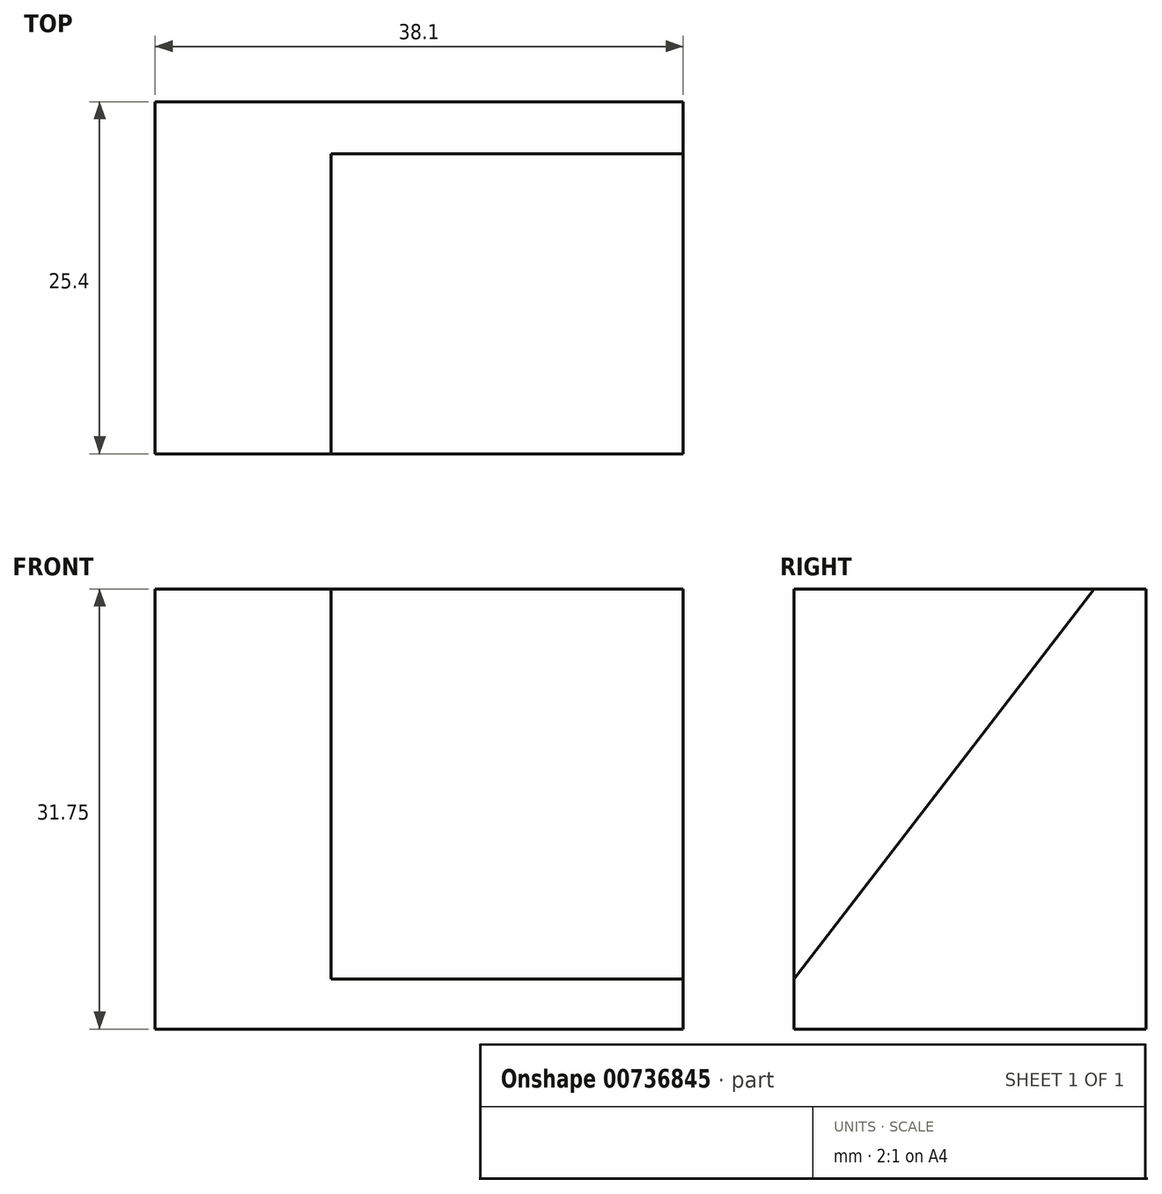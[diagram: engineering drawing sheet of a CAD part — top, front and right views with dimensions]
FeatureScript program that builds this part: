
annotation { "Feature Type Name" : "Feature", "Feature Type Description" : "" }
export const myFeature = defineFeature(function(context is Context, id is Id, definition is map)
    precondition{}
    {
        {
            var Q0;
            Q0=qCreatedBy(makeId("Right.planeOp"),FACE);
            var sketch = newSketch(context, id + "F0", { "sketchPlane" : qUnion([Q0])});
            skLineSegment(sketch, "E0", {"start": v(0, 0) * mm, "end": v(25.4, 0) * mm});
            skLineSegment(sketch, "E1", {"start": v(25.4, 0) * mm, "end": v(25.4, 31.75) * mm});
            skLineSegment(sketch, "E2", {"start": v(25.4, 31.75) * mm, "end": v(0, 31.75) * mm});
            skLineSegment(sketch, "E3", {"start": v(0, 31.75) * mm, "end": v(0, 0) * mm});
            skLineSegment(sketch, "E4", {"start": v(-0.76, 1.48) * mm, "end": v(0, 0) * mm});
            skSolve(sketch);
        }
        {
            var Q0;
            Q0=makeQuery(id+"F0.imprint","IMPRINT",FACE,{"disambiguationData":[TD([[makeQuery(id+"F0.imprint","IMPRINT",EDGE,{"derivedFrom":sQuery(id+"F0.wireOp",EDGE,"E0")}),1.0]])]});
            extrude(context, id + "F1", {"entities" : qUnion([Q0]), "depth" : 38.1 * mm, "offsetDistance" : 25.4 * mm});
        }
        {
            var Q0;
            Q0=makeQuery(id+"F1.opExtrude","CAP_FACE",FACE,{"disambiguationData":[OSD([sQuery(id+"F0.wireOp",EDGE,"E0"),sQuery(id+"F0.wireOp",EDGE,"E1"),sQuery(id+"F0.wireOp",EDGE,"E2"),sQuery(id+"F0.wireOp",EDGE,"E3")])],"isStart":false});
            var sketch = newSketch(context, id + "F2", { "sketchPlane" : qUnion([Q0])});
            skLineSegment(sketch, "E5", {"start": v(21.65, 31.75) * mm, "end": v(0, 3.6) * mm});
            skSolve(sketch);
        }
        {
            var Q0;
            {var subQ0=sQuery(id+"F2.wireOp",EDGE,"E5");Q0=makeQuery(id+"F2.imprint","IMPRINT",FACE,{"disambiguationData":[TD([[makeQuery(id+"F2.imprint","IMPRINT",EDGE,{"derivedFrom":subQ0}),-1.0]])]});}
            extrude(context, id + "F3", {"entities" : qUnion([Q0]), "operationType" : NewBodyOperationType.REMOVE, "oppositeDirection" : true, "depth" : 25.4 * mm, "offsetDistance" : 25.4 * mm});
        }
    });
